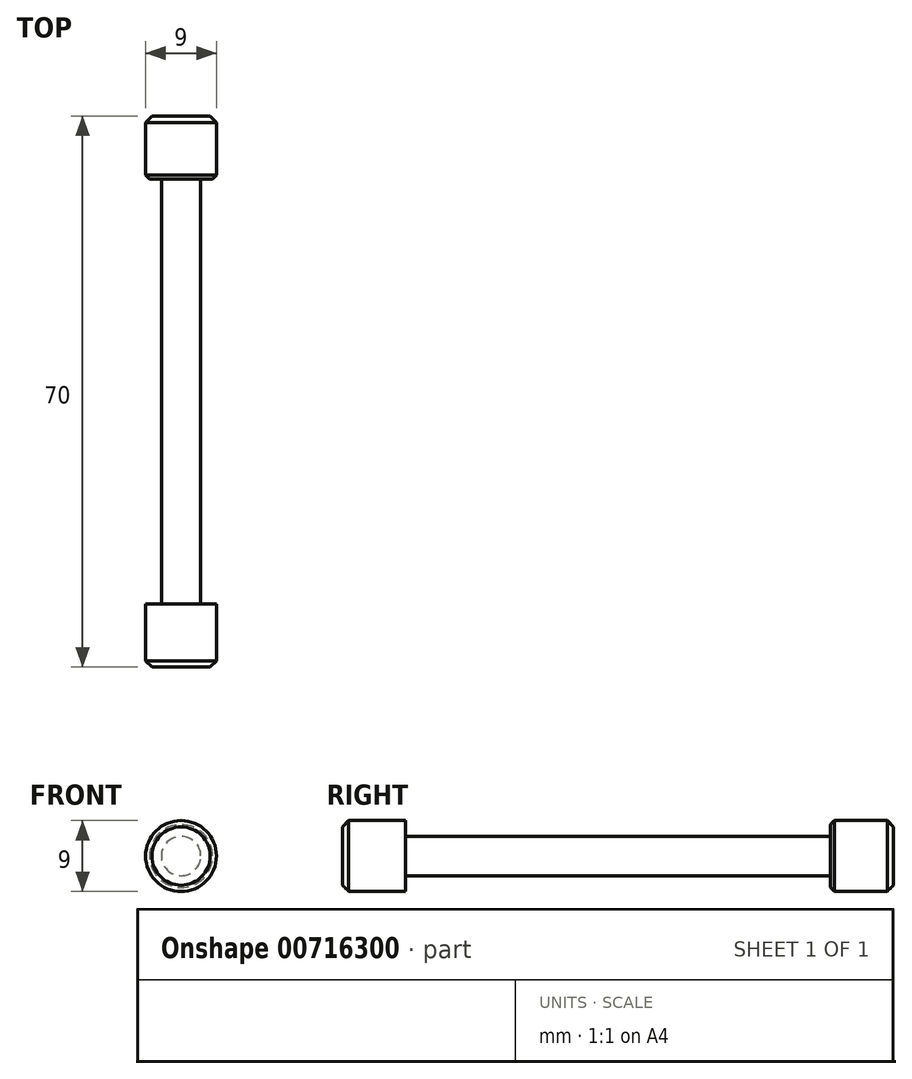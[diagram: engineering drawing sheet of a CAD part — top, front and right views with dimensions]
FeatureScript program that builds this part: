
annotation { "Feature Type Name" : "Feature", "Feature Type Description" : "" }
export const myFeature = defineFeature(function(context is Context, id is Id, definition is map)
    precondition{}
    {
        {
            var Q0;
            Q0=qCreatedBy(makeId("Front.planeOp"),FACE);
            var sketch = newSketch(context, id + "F0", { "sketchPlane" : qUnion([Q0])});
            skCircle(sketch, "E0", {"center": v(0, 0) * mm, "radius": 4.5 * mm});
            skCircle(sketch, "E1", {"center": v(0, 0) * mm, "radius": 2.5 * mm});
            skSolve(sketch);
        }
        {
            var Q0;
            Q0=makeQuery(id+"F0.imprint","IMPRINT",FACE,{"disambiguationData":[TD([[makeQuery(id+"F0.imprint","IMPRINT",EDGE,{"derivedFrom":sQuery(id+"F0.wireOp",EDGE,"E0")}),1.0]])]});
            var Q1;
            Q1=makeQuery(id+"F0.imprint","IMPRINT",FACE,{"disambiguationData":[TD([[makeQuery(id+"F0.imprint","IMPRINT",EDGE,{"derivedFrom":sQuery(id+"F0.wireOp",EDGE,"E1")}),1.0]])]});
            extrude(context, id + "F1", {"entities" : qUnion([Q0, Q1]), "endBound" : BoundingType.SYMMETRIC, "depth" : 70 * mm, "offsetDistance" : 25 * mm});
        }
        {
            var Q0;
            Q0=makeQuery(id+"F0.imprint","IMPRINT",FACE,{"disambiguationData":[TD([[makeQuery(id+"F0.imprint","IMPRINT",EDGE,{"derivedFrom":sQuery(id+"F0.wireOp",EDGE,"E0")}),1.0]])]});
            extrude(context, id + "F2", {"entities" : qUnion([Q0]), "operationType" : NewBodyOperationType.REMOVE, "endBound" : BoundingType.SYMMETRIC, "oppositeDirection" : true, "depth" : 54 * mm, "offsetDistance" : 25 * mm});
        }
        {
            var Q0;
            Q0=makeQuery(id+"F1.opExtrude","CAP_EDGE",EDGE,{"disambiguationData":[OSD([sQuery(id+"F0.wireOp",EDGE,"E0")])],"isStart":true});
            var Q1;
            Q1=makeQuery(id+"F1.opExtrude","CAP_EDGE",EDGE,{"disambiguationData":[OSD([sQuery(id+"F0.wireOp",EDGE,"E0")])],"isStart":false});
            chamfer(context, id + "F3", {"entities" : qUnion([Q0, Q1]), "width" : 0.8 * mm, "tangentPropagation" : true});
        }
        {
            var Q0;
            Q0=makeQuery(id+"F2.boolean.opBoolean","COPY",EDGE,{"derivedFrom":makeQuery(id+"F2.opExtrude","CAP_EDGE",EDGE,{"disambiguationData":[OSD([sQuery(id+"F0.wireOp",EDGE,"E0")])],"isStart":true})});
            var Q1;
            Q1=makeQuery(id+"F2.boolean.opBoolean","COPY",EDGE,{"derivedFrom":makeQuery(id+"F2.opExtrude","CAP_EDGE",EDGE,{"disambiguationData":[OSD([sQuery(id+"F0.wireOp",EDGE,"E0")])],"isStart":false})});
            chamfer(context, id + "F4", {"entities" : qUnion([Q0, Q1]), "width" : 0.5 * mm, "tangentPropagation" : true});
        }
    });
